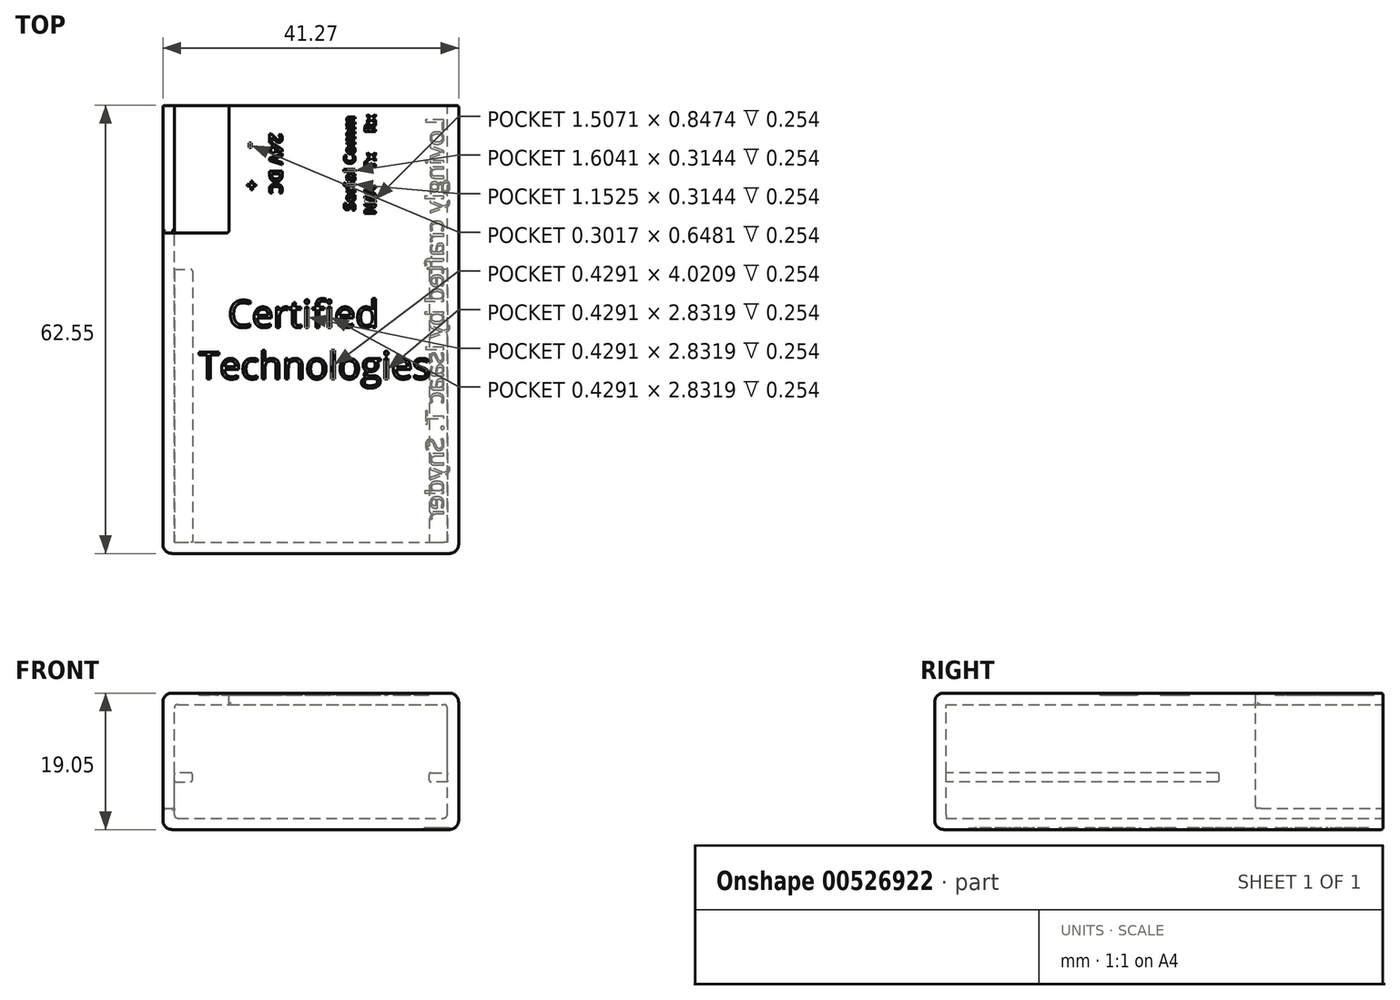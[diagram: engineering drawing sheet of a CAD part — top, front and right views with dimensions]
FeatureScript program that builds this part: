
annotation { "Feature Type Name" : "Feature", "Feature Type Description" : "" }
export const myFeature = defineFeature(function(context is Context, id is Id, definition is map)
    precondition{}
    {
        {
            var Q0;
            Q0=qCreatedBy(makeId("Top.planeOp"),FACE);
            var sketch = newSketch(context, id + "F0", { "sketchPlane" : qUnion([Q0])});
            skLineSegment(sketch, "E0", {"start": v(-24.36, 42.34) * mm, "end": v(13.74, 42.34) * mm});
            skLineSegment(sketch, "E1", {"start": v(13.74, 42.34) * mm, "end": v(13.74, -18.62) * mm});
            skLineSegment(sketch, "E2", {"start": v(13.74, -18.62) * mm, "end": v(-24.36, -18.62) * mm});
            skLineSegment(sketch, "E3", {"start": v(-24.36, -18.62) * mm, "end": v(-24.36, 42.34) * mm});
            skLineSegment(sketch, "E4.1", {"start": v(-25.95, -20.21) * mm, "end": v(-25.95, 42.34) * mm});
            skLineSegment(sketch, "E4.2", {"start": v(15.32, -20.21) * mm, "end": v(-25.95, -20.21) * mm});
            skLineSegment(sketch, "E4.3", {"start": v(15.32, 42.34) * mm, "end": v(15.32, -20.21) * mm});
            skLineSegment(sketch, "E5", {"start": v(-24.36, 42.34) * mm, "end": v(-25.95, 42.34) * mm});
            skLineSegment(sketch, "E6", {"start": v(13.74, 42.34) * mm, "end": v(15.32, 42.34) * mm});
            skSolve(sketch);
        }
        {
            var Q0;
            Q0=makeQuery(id+"F0.imprint","IMPRINT",FACE,{"disambiguationData":[TD([[makeQuery(id+"F0.imprint","IMPRINT",EDGE,{"derivedFrom":sQuery(id+"F0.wireOp",EDGE,"E1")}),1.0]])]});
            var Q1;
            Q1=makeQuery(id+"F0.imprint","IMPRINT",FACE,{"disambiguationData":[TD([[makeQuery(id+"F0.imprint","IMPRINT",EDGE,{"derivedFrom":sQuery(id+"F0.wireOp",EDGE,"E0")}),-1.0]])]});
            extrude(context, id + "F1", {"entities" : qUnion([Q0, Q1]), "oppositeDirection" : true, "depth" : 19.05 * mm, "offsetDistance" : 25.4 * mm});
        }
        {
            var Q0;
            Q0=makeQuery(id+"F1.opExtrude","SWEPT_FACE",FACE,{"disambiguationData":[OSD([sQuery(id+"F0.wireOp",EDGE,"E0"),sQuery(id+"F0.wireOp",EDGE,"E5"),sQuery(id+"F0.wireOp",EDGE,"E6")])]});
            var sketch = newSketch(context, id + "F2", { "sketchPlane" : qUnion([Q0])});
            skPoint(sketch, "E7.0", {"position": v(24.36, 0) * mm});
            skPoint(sketch, "E7.1", {"position": v(-13.74, 0) * mm});
            skLineSegment(sketch, "E8", {"start": v(24.36, -1.59) * mm, "end": v(-13.74, -1.59) * mm});
            skLineSegment(sketch, "E9", {"start": v(24.36, -17.46) * mm, "end": v(-13.74, -17.46) * mm});
            skLineSegment(sketch, "E10", {"start": v(24.36, -17.46) * mm, "end": v(24.36, -1.59) * mm});
            skLineSegment(sketch, "E11", {"start": v(-13.74, -17.46) * mm, "end": v(-13.74, -1.59) * mm});
            skSolve(sketch);
        }
        {
            var Q0;
            Q0=makeQuery(id+"F2.imprint","IMPRINT",FACE,{"disambiguationData":[TD([[makeQuery(id+"F2.imprint","IMPRINT",EDGE,{"derivedFrom":sQuery(id+"F2.wireOp",EDGE,"E8")}),1.0]])]});
            extrude(context, id + "F3", {"entities" : qUnion([Q0]), "operationType" : NewBodyOperationType.REMOVE, "oppositeDirection" : true, "depth" : 60.96 * mm, "offsetDistance" : 25.4 * mm});
        }
        {
            var Q0;
            Q0=makeQuery(id+"F1.opExtrude","CAP_EDGE",EDGE,{"disambiguationData":[OSD([sQuery(id+"F0.wireOp",EDGE,"E4.1")])],"isStart":true});
            var Q1;
            Q1=makeQuery(id+"F1.opExtrude","CAP_EDGE",EDGE,{"disambiguationData":[OSD([sQuery(id+"F0.wireOp",EDGE,"E4.3")])],"isStart":true});
            var Q2;
            Q2=makeQuery(id+"F1.opExtrude","CAP_EDGE",EDGE,{"disambiguationData":[OSD([sQuery(id+"F0.wireOp",EDGE,"E4.3")])],"isStart":false});
            var Q3;
            Q3=makeQuery(id+"F1.opExtrude","CAP_EDGE",EDGE,{"disambiguationData":[OSD([sQuery(id+"F0.wireOp",EDGE,"E4.1")])],"isStart":false});
            var Q4;
            Q4=makeQuery(id+"F1.opExtrude","SWEPT_EDGE",EDGE,{"disambiguationData":[OSD([sQuery(id+"F0.wireOp",EDGE,"E4.1"),sQuery(id+"F0.wireOp",EDGE,"E4.2")])]});
            var Q5;
            Q5=makeQuery(id+"F1.opExtrude","CAP_EDGE",EDGE,{"disambiguationData":[OSD([sQuery(id+"F0.wireOp",EDGE,"E4.2")])],"isStart":false});
            var Q6;
            Q6=makeQuery(id+"F1.opExtrude","CAP_EDGE",EDGE,{"disambiguationData":[OSD([sQuery(id+"F0.wireOp",EDGE,"E4.2")])],"isStart":true});
            var Q7;
            Q7=makeQuery(id+"F1.opExtrude","SWEPT_EDGE",EDGE,{"disambiguationData":[OSD([sQuery(id+"F0.wireOp",EDGE,"E4.2"),sQuery(id+"F0.wireOp",EDGE,"E4.3")])]});
            fillet(context, id + "F4", {"entities" : qUnion([Q0, Q1, Q2, Q3, Q4, Q5, Q6, Q7]), "radius" : 1.27 * mm, "tangentPropagation" : true, "allowEdgeOverflow" : false});
        }
        {
            var Q0;
            Q0=makeQuery(id+"F3.boolean.opBoolean","COPY",FACE,{"derivedFrom":makeQuery(id+"F3.opExtrude","CAP_FACE",FACE,{"disambiguationData":[OSD([sQuery(id+"F2.wireOp",EDGE,"E8"),sQuery(id+"F2.wireOp",EDGE,"E9"),sQuery(id+"F2.wireOp",EDGE,"E10"),sQuery(id+"F2.wireOp",EDGE,"E11")])],"isStart":false})});
            var sketch = newSketch(context, id + "F5", { "sketchPlane" : qUnion([Q0])});
            skLineSegment(sketch, "E12", {"start": v(24.36, -17.46) * mm, "end": v(24.36, -12.38) * mm, "construction": true});
            skLineSegment(sketch, "E13", {"start": v(24.36, -12.38) * mm, "end": v(21.82, -12.38) * mm});
            skLineSegment(sketch, "E14", {"start": v(21.82, -12.38) * mm, "end": v(21.82, -11.11) * mm});
            skLineSegment(sketch, "E15", {"start": v(21.82, -11.11) * mm, "end": v(24.36, -11.11) * mm});
            skLineSegment(sketch, "E16", {"start": v(-13.74, -17.46) * mm, "end": v(-13.74, -12.38) * mm, "construction": true});
            skLineSegment(sketch, "E17", {"start": v(-13.74, -12.38) * mm, "end": v(-11.2, -12.38) * mm});
            skLineSegment(sketch, "E18", {"start": v(-11.2, -12.38) * mm, "end": v(-11.2, -11.11) * mm});
            skLineSegment(sketch, "E19", {"start": v(-11.2, -11.11) * mm, "end": v(-13.74, -11.11) * mm});
            skSolve(sketch);
        }
        {
            var Q0;
            Q0=makeQuery(id+"F3.boolean.opBoolean","COPY",EDGE,{"derivedFrom":makeQuery(id+"F3.opExtrude","SWEPT_EDGE",EDGE,{"disambiguationData":[OSD([sQuery(id+"F2.wireOp",EDGE,"E9"),sQuery(id+"F2.wireOp",EDGE,"E10")])]})});
            var Q1;
            Q1=makeQuery(id+"F3.boolean.opBoolean","COPY",EDGE,{"derivedFrom":makeQuery(id+"F3.opExtrude","SWEPT_EDGE",EDGE,{"disambiguationData":[OSD([sQuery(id+"F2.wireOp",EDGE,"E9"),sQuery(id+"F2.wireOp",EDGE,"E11")])]})});
            var Q2;
            Q2=makeQuery(id+"F3.boolean.opBoolean","COPY",EDGE,{"derivedFrom":makeQuery(id+"F3.opExtrude","SWEPT_EDGE",EDGE,{"disambiguationData":[OSD([sQuery(id+"F2.wireOp",EDGE,"E8"),sQuery(id+"F2.wireOp",EDGE,"E10")])]})});
            var Q3;
            Q3=makeQuery(id+"F3.boolean.opBoolean","COPY",EDGE,{"derivedFrom":makeQuery(id+"F3.opExtrude","SWEPT_EDGE",EDGE,{"disambiguationData":[OSD([sQuery(id+"F2.wireOp",EDGE,"E8"),sQuery(id+"F2.wireOp",EDGE,"E11")])]})});
            fillet(context, id + "F6", {"entities" : qUnion([Q0, Q1, Q2, Q3]), "radius" : 0.5 * mm, "tangentPropagation" : true, "allowEdgeOverflow" : false});
        }
        {
            var Q0;
            Q0=makeQuery(id+"F1.opExtrude","SWEPT_FACE",FACE,{"disambiguationData":[OSD([sQuery(id+"F0.wireOp",EDGE,"E0"),sQuery(id+"F0.wireOp",EDGE,"E5"),sQuery(id+"F0.wireOp",EDGE,"E6")])]});
            var sketch = newSketch(context, id + "F7", { "sketchPlane" : qUnion([Q0])});
            skLineSegment(sketch, "E20", {"start": v(-6.12, -2.1) * mm, "end": v(-6.12, 0) * mm});
            skLineSegment(sketch, "E21", {"start": v(-6.12, 0) * mm, "end": v(-13.74, 0) * mm});
            skLineSegment(sketch, "E22", {"start": v(-15.32, -2.1) * mm, "end": v(-15.32, 0) * mm});
            skLineSegment(sketch, "E23", {"start": v(-15.32, 0) * mm, "end": v(-13.74, 0) * mm});
            skPoint(sketch, "E24.end.orphan", {"position": v(25.95, -16.07) * mm});
            skPoint(sketch, "E25.start.orphan", {"position": v(25.95, -2.1) * mm});
            skLineSegment(sketch, "E26", {"start": v(25.95, 0) * mm, "end": v(25.95, -16.07) * mm});
            skPoint(sketch, "E27.endSnap0", {"position": v(16.74, -1.05) * mm});
            skLineSegment(sketch, "E28", {"start": v(25.95, -16.07) * mm, "end": v(16.74, -16.07) * mm});
            skPoint(sketch, "E29.end.orphan", {"position": v(24.36, 0) * mm});
            skLineSegment(sketch, "E30", {"start": v(16.74, 0) * mm, "end": v(25.95, 0) * mm});
            skPoint(sketch, "E27.start.orphan", {"position": v(16.74, -2.1) * mm});
            skLineSegment(sketch, "E31", {"start": v(16.74, -16.07) * mm, "end": v(16.74, 0) * mm});
            skLineSegment(sketch, "E32", {"start": v(-6.12, 0) * mm, "end": v(-6.12, -16.07) * mm});
            skLineSegment(sketch, "E33", {"start": v(-6.12, -16.07) * mm, "end": v(-15.32, -16.07) * mm});
            skLineSegment(sketch, "E34", {"start": v(-15.32, -16.07) * mm, "end": v(-15.32, 0) * mm});
            skSolve(sketch);
        }
        {
            var Q0;
            Q0=makeQuery(id+"F1.opExtrude","CAP_FACE",FACE,{"disambiguationData":[OSD([sQuery(id+"F0.wireOp",EDGE,"E0"),sQuery(id+"F0.wireOp",EDGE,"E4.1"),sQuery(id+"F0.wireOp",EDGE,"E4.2"),sQuery(id+"F0.wireOp",EDGE,"E4.3"),sQuery(id+"F0.wireOp",EDGE,"E5"),sQuery(id+"F0.wireOp",EDGE,"E6")])],"isStart":true});
            var sketch = newSketch(context, id + "F8", { "sketchPlane" : qUnion([Q0])});
            skText(sketch, "E35", { "text": "24V DC\n  -       +", "fontName": "OpenSans-Bold.ttf"});
            skText(sketch, "E36", { "text": " Serial Comm\nN/A    Tx     Rx", "fontName": "OpenSans-Bold.ttf"});
            skLineSegment(sketch, "E37", {"start": v(-9.28, 34.18) * mm, "end": v(-0.65, 34.18) * mm, "construction": true});
            skText(sketch, "E38", { "text": "   Certified\nTechnologies", "fontName": "OpenSans-Regular.ttf"});
            skLineSegment(sketch, "E39", {"start": v(-5.31, -18.94) * mm, "end": v(-5.31, 11.34) * mm, "construction": true});
            const initialGuessF8  = {"E35": [-0.01106, 0.03845, 0, -1, 0.00178], "E36": [0.00087, 0.02708, 0, 1, 0.00152], "E38": [-0.02098, 0.01134, 1, 0, 0.00381]};
            skSetInitialGuess(sketch, initialGuessF8);
            skSolve(sketch);
        }
        {
            var Q0;
            Q0 = qSketchRegion(id + "F8", true);
            extrude(context, id + "F9", {"entities" : qUnion([Q0]), "operationType" : NewBodyOperationType.REMOVE, "oppositeDirection" : true, "depth" : 0.25 * mm, "offsetDistance" : 25.4 * mm});
        }
        {
            var Q0;
            Q0=makeQuery(id+"F1.opExtrude","CAP_FACE",FACE,{"disambiguationData":[OSD([sQuery(id+"F0.wireOp",EDGE,"E0"),sQuery(id+"F0.wireOp",EDGE,"E4.1"),sQuery(id+"F0.wireOp",EDGE,"E4.2"),sQuery(id+"F0.wireOp",EDGE,"E4.3"),sQuery(id+"F0.wireOp",EDGE,"E5"),sQuery(id+"F0.wireOp",EDGE,"E6")])],"isStart":false});
            var sketch = newSketch(context, id + "F10", { "sketchPlane" : qUnion([Q0])});
            skText(sketch, "E40", { "text": "Lovingly crafted by Isaac T. Snyder", "fontName": "OpenSans-Regular.ttf"});
            skLineSegment(sketch, "E41", {"start": v(14.05, -11.7) * mm, "end": v(13.25, -11.7) * mm, "construction": true});
            const initialGuessF10  = {"E40": [0.01325, -0.04068, 0, 1, 0.00254]};
            skSetInitialGuess(sketch, initialGuessF10);
            skSolve(sketch);
        }
        {
            var Q0;
            Q0 = qSketchRegion(id + "F10", true);
            extrude(context, id + "F11", {"entities" : qUnion([Q0]), "operationType" : NewBodyOperationType.REMOVE, "oppositeDirection" : true, "depth" : 0.25 * mm, "offsetDistance" : 25.4 * mm});
        }
        {
            var Q0;
            {var subQ0=sQuery(id+"F5.wireOp",EDGE,"E13");Q0=makeQuery(id+"F5.imprint","IMPRINT",FACE,{"disambiguationData":[TD([[makeQuery(id+"F5.imprint","IMPRINT",EDGE,{"derivedFrom":subQ0}),-1.0]])]});}
            var Q1;
            {var subQ0=sQuery(id+"F5.wireOp",EDGE,"E17");Q1=makeQuery(id+"F5.imprint","IMPRINT",FACE,{"disambiguationData":[TD([[makeQuery(id+"F5.imprint","IMPRINT",EDGE,{"derivedFrom":subQ0}),1.0]])]});}
            extrude(context, id + "F12", {"entities" : qUnion([Q0, Q1]), "operationType" : NewBodyOperationType.ADD, "depth" : 38.1 * mm, "offsetDistance" : 25.4 * mm});
        }
        {
            var Q0;
            Q0=makeQuery(id+"F12.opExtrude","SWEPT_EDGE",EDGE,{"disambiguationData":[OSD([sQuery(id+"F5.wireOp",EDGE,"E13"),sQuery(id+"F5.wireOp",EDGE,"E14")])]});
            var Q1;
            Q1=makeQuery(id+"F12.opExtrude","SWEPT_EDGE",EDGE,{"disambiguationData":[OSD([sQuery(id+"F5.wireOp",EDGE,"E14"),sQuery(id+"F5.wireOp",EDGE,"E15")])]});
            var Q2;
            Q2=makeQuery(id+"F12.opExtrude","CAP_EDGE",EDGE,{"disambiguationData":[OSD([sQuery(id+"F5.wireOp",EDGE,"E14")])],"isStart":true});
            var Q3;
            Q3=makeQuery(id+"F12.opExtrude","SWEPT_EDGE",EDGE,{"disambiguationData":[OSD([sQuery(id+"F5.wireOp",EDGE,"E18"),sQuery(id+"F5.wireOp",EDGE,"E19")])]});
            var Q4;
            Q4=makeQuery(id+"F12.opExtrude","SWEPT_EDGE",EDGE,{"disambiguationData":[OSD([sQuery(id+"F5.wireOp",EDGE,"E17"),sQuery(id+"F5.wireOp",EDGE,"E18")])]});
            var Q5;
            Q5=makeQuery(id+"F12.opExtrude","CAP_EDGE",EDGE,{"disambiguationData":[OSD([sQuery(id+"F5.wireOp",EDGE,"E18")])],"isStart":true});
            var Q6;
            Q6=makeQuery(id+"F12.opExtrude","SWEPT_EDGE",EDGE,{"disambiguationData":[OSD([sQuery(id+"F2.wireOp",EDGE,"E10"),sQuery(id+"F5.wireOp",EDGE,"E15")])]});
            var Q7;
            Q7=makeQuery(id+"F12.opExtrude","CAP_EDGE",EDGE,{"disambiguationData":[OSD([sQuery(id+"F2.wireOp",EDGE,"E10")])],"isStart":false});
            var Q8;
            Q8=makeQuery(id+"F12.opExtrude","CAP_EDGE",EDGE,{"disambiguationData":[OSD([sQuery(id+"F5.wireOp",EDGE,"E15")])],"isStart":false});
            var Q9;
            Q9=makeQuery(id+"F12.opExtrude","CAP_EDGE",EDGE,{"disambiguationData":[OSD([sQuery(id+"F5.wireOp",EDGE,"E14")])],"isStart":false});
            var Q10;
            Q10=makeQuery(id+"F12.opExtrude","CAP_EDGE",EDGE,{"disambiguationData":[OSD([sQuery(id+"F5.wireOp",EDGE,"E13")])],"isStart":false});
            var Q11;
            Q11=makeQuery(id+"F12.opExtrude","CAP_EDGE",EDGE,{"disambiguationData":[OSD([sQuery(id+"F5.wireOp",EDGE,"E19")])],"isStart":false});
            var Q12;
            Q12=makeQuery(id+"F12.opExtrude","CAP_EDGE",EDGE,{"disambiguationData":[OSD([sQuery(id+"F2.wireOp",EDGE,"E11")])],"isStart":false});
            var Q13;
            Q13=makeQuery(id+"F12.opExtrude","CAP_EDGE",EDGE,{"disambiguationData":[OSD([sQuery(id+"F5.wireOp",EDGE,"E17")])],"isStart":false});
            var Q14;
            Q14=makeQuery(id+"F12.opExtrude","SWEPT_EDGE",EDGE,{"disambiguationData":[OSD([sQuery(id+"F2.wireOp",EDGE,"E11"),sQuery(id+"F5.wireOp",EDGE,"E17")])]});
            var Q15;
            Q15=makeQuery(id+"F12.opExtrude","CAP_EDGE",EDGE,{"disambiguationData":[OSD([sQuery(id+"F5.wireOp",EDGE,"E18")])],"isStart":false});
            fillet(context, id + "F13", {"entities" : qUnion([Q0, Q1, Q2, Q3, Q4, Q5, Q6, Q7, Q8, Q9, Q10, Q11, Q12, Q13, Q14, Q15]), "radius" : 0.25 * mm, "tangentPropagation" : true, "allowEdgeOverflow" : false});
        }
        {
            var Q0;
            {var subQ1=sQuery(id+"F0.wireOp",EDGE,"E6");var subQ2=sQuery(id+"F0.wireOp",EDGE,"E5");var subQ3=sQuery(id+"F0.wireOp",EDGE,"E0");var subQ4=makeQuery(id+"F1.opExtrude","SWEPT_FACE",FACE,{"disambiguationData":[OSD([subQ3,subQ2,subQ1])]});var subQ5=sQuery(id+"F0.wireOp",EDGE,"E4.1");var subQ6=makeQuery(id+"F4.opFillet","BLEND_EDGE",EDGE,{"blendedFrom":[makeQuery(id+"F1.opExtrude","CAP_EDGE",EDGE,{"disambiguationData":[OSD([subQ5])],"isStart":true}),subQ4],"blendedInto":[subQ4]});Q0=makeQuery(id+"F7.imprint","IMPRINT",FACE,{"disambiguationData":[TD([[makeQuery(id+"F7.imprint","IMPRINT",EDGE,{"derivedFrom":subQ6}),1.0]])]});}
            var Q1;
            {var subQ1=sQuery(id+"F7.wireOp",EDGE,"E21");Q1=makeQuery(id+"F7.imprint","IMPRINT",FACE,{"disambiguationData":[TD([[makeQuery(id+"F7.imprint","IMPRINT",EDGE,{"derivedFrom":subQ1}),1.0]])]});}
            extrude(context, id + "F14", {"entities" : qUnion([Q0, Q1]), "operationType" : NewBodyOperationType.REMOVE, "oppositeDirection" : true, "depth" : 17.78 * mm, "offsetDistance" : 25.4 * mm});
        }
        {
            var Q0;
            Q0=makeQuery(id+"F14.boolean.opBoolean","COPY",FACE,{"derivedFrom":makeQuery(id+"F14.opExtrude","CAP_FACE",FACE,{"disambiguationData":[OSD([sQuery(id+"F0.wireOp",EDGE,"E0"),sQuery(id+"F0.wireOp",EDGE,"E4.3"),sQuery(id+"F0.wireOp",EDGE,"E5"),sQuery(id+"F0.wireOp",EDGE,"E6"),sQuery(id+"F2.wireOp",EDGE,"E8"),sQuery(id+"F2.wireOp",EDGE,"E11"),sQuery(id+"F7.wireOp",EDGE,"E21"),sQuery(id+"F7.wireOp",EDGE,"E23"),sQuery(id+"F7.wireOp",EDGE,"E32"),sQuery(id+"F7.wireOp",EDGE,"E33"),sQuery(id+"F7.wireOp",EDGE,"E34")])],"isStart":false})});
            var Q1;
            {var subQ0=sQuery(id+"F0.wireOp",EDGE,"E6");var subQ1=sQuery(id+"F0.wireOp",EDGE,"E5");var subQ2=sQuery(id+"F0.wireOp",EDGE,"E0");Q1=makeQuery(id+"F14.boolean.opBoolean","SPLIT",FACE,{"disambiguationData":[TD([makeQuery(id+"F3.boolean.opBoolean","COPY",FACE,{"derivedFrom":makeQuery(id+"F3.opExtrude","SWEPT_FACE",FACE,{"disambiguationData":[OSD([sQuery(id+"F2.wireOp",EDGE,"E8")])]})})])],"derivedFrom":makeQuery(id+"F1.opExtrude","SWEPT_FACE",FACE,{"disambiguationData":[OSD([subQ2,subQ1,subQ0])]})});}
            var Q2;
            Q2=makeQuery(id+"F14.boolean.opBoolean","COPY",FACE,{"derivedFrom":makeQuery(id+"F14.opExtrude","CAP_FACE",FACE,{"disambiguationData":[OSD([sQuery(id+"F0.wireOp",EDGE,"E0"),sQuery(id+"F0.wireOp",EDGE,"E4.1"),sQuery(id+"F0.wireOp",EDGE,"E5"),sQuery(id+"F0.wireOp",EDGE,"E6"),sQuery(id+"F2.wireOp",EDGE,"E8"),sQuery(id+"F2.wireOp",EDGE,"E10"),sQuery(id+"F7.wireOp",EDGE,"E26"),sQuery(id+"F7.wireOp",EDGE,"E28"),sQuery(id+"F7.wireOp",EDGE,"E30"),sQuery(id+"F7.wireOp",EDGE,"E31")])],"isStart":false})});
            var Q3;
            {var subQ2=sQuery(id+"F0.wireOp",EDGE,"E4.1");var subQ4=sQuery(id+"F0.wireOp",EDGE,"E6");var subQ5=sQuery(id+"F0.wireOp",EDGE,"E5");var subQ7=sQuery(id+"F0.wireOp",EDGE,"E0");Q3=makeQuery(id+"F14.boolean.opBoolean","SPLIT",FACE,{"disambiguationData":[TD([makeQuery(id+"F1.opExtrude","SWEPT_FACE",FACE,{"disambiguationData":[OSD([subQ2])]})])],"derivedFrom":makeQuery(id+"F1.opExtrude","SWEPT_FACE",FACE,{"disambiguationData":[OSD([subQ7,subQ5,subQ4])]})});}
            fillet(context, id + "F15", {"entities" : qUnion([Q0, Q1, Q2, Q3]), "radius" : 0.25 * mm, "tangentPropagation" : true, "allowEdgeOverflow" : false});
        }
    });
